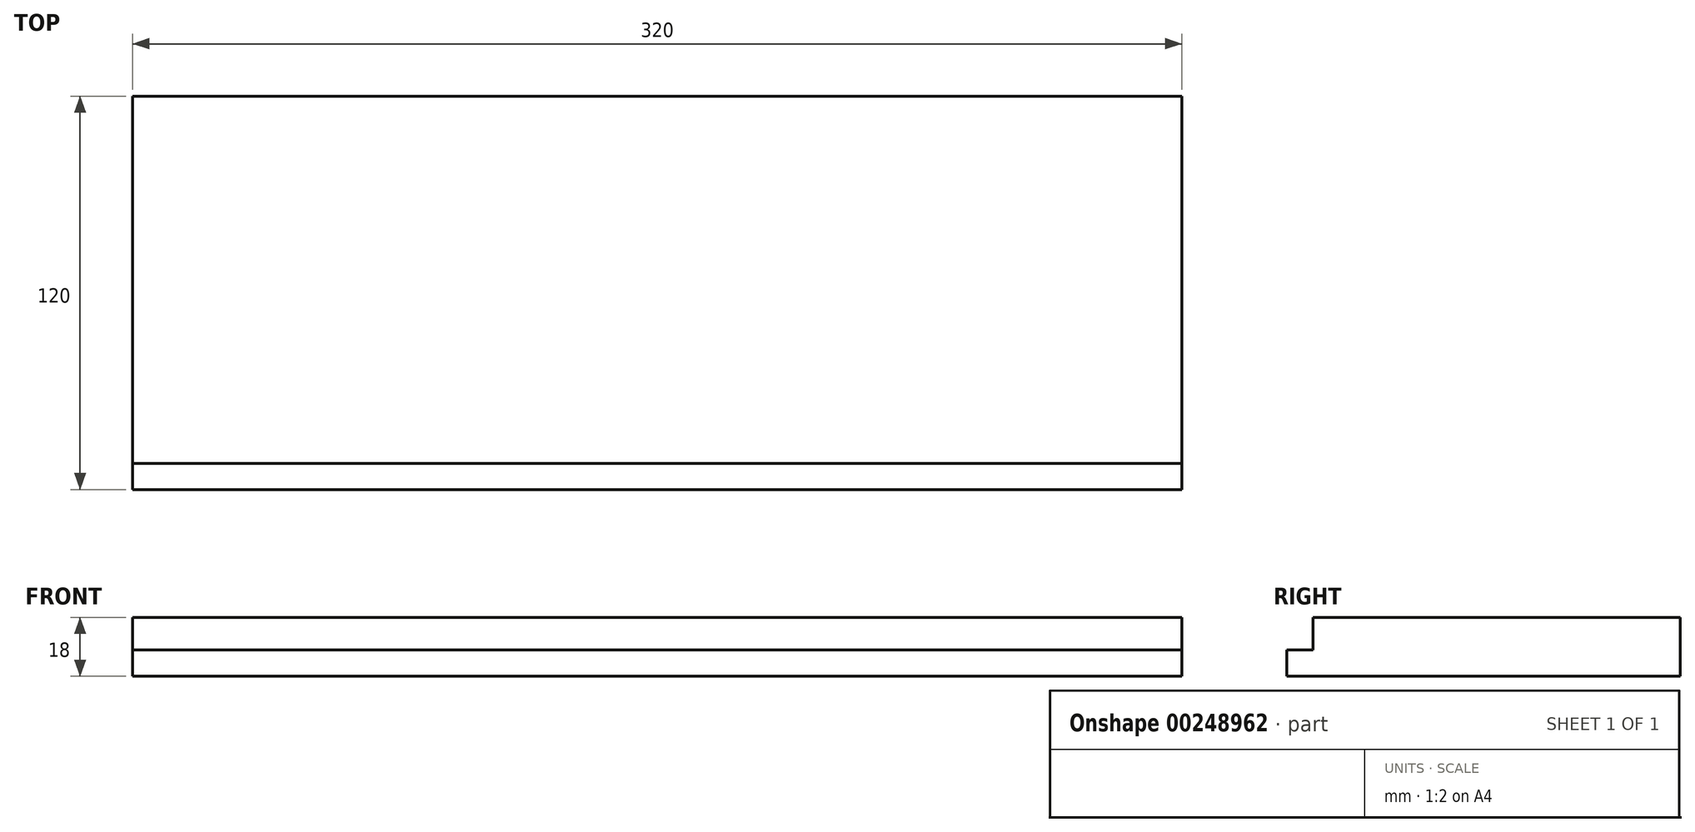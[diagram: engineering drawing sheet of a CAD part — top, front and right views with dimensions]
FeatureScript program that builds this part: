
annotation { "Feature Type Name" : "Feature", "Feature Type Description" : "" }
export const myFeature = defineFeature(function(context is Context, id is Id, definition is map)
    precondition{}
    {
        {
            var Q0;
            Q0=qCreatedBy(makeId("Top.planeOp"),FACE);
            var sketch = newSketch(context, id + "F0", { "sketchPlane" : qUnion([Q0])});
            skLineSegment(sketch, "E0.bottom", {"start": v(-160, -60) * mm, "end": v(160, -60) * mm});
            skLineSegment(sketch, "E0.top", {"start": v(-160, 60) * mm, "end": v(160, 60) * mm});
            skLineSegment(sketch, "E0.left", {"start": v(-160, 60) * mm, "end": v(-160, -60) * mm});
            skLineSegment(sketch, "E0.right", {"start": v(160, 60) * mm, "end": v(160, -60) * mm});
            skPoint(sketch, "E1", {"position": v(160, 0) * mm});
            skPoint(sketch, "E2", {"position": v(0, 60) * mm});
            skSolve(sketch);
        }
        {
            var Q0;
            Q0 = qSketchRegion(id + "F0", true);
            extrude(context, id + "F1", {"entities" : qUnion([Q0]), "depth" : 18 * mm});
        }
        {
            var Q0;
            Q0=makeQuery(id+"F1.opExtrude","SWEPT_FACE",FACE,{"disambiguationData":[OSD([sQuery(id+"F0.wireOp",EDGE,"E0.bottom")])]});
            var sketch = newSketch(context, id + "F2", { "sketchPlane" : qUnion([Q0])});
            skLineSegment(sketch, "E3.0", {"start": v(-160, 18) * mm, "end": v(160, 18) * mm});
            skLineSegment(sketch, "E4", {"start": v(-160, 18) * mm, "end": v(-160, 8) * mm});
            skLineSegment(sketch, "E5", {"start": v(-160, 8) * mm, "end": v(160, 8) * mm});
            skLineSegment(sketch, "E6", {"start": v(160, 8) * mm, "end": v(160, 18) * mm});
            skSolve(sketch);
        }
        {
            var Q0;
            Q0 = qSketchRegion(id + "F2", true);
            extrude(context, id + "F3", {"entities" : qUnion([Q0]), "operationType" : NewBodyOperationType.REMOVE, "oppositeDirection" : true, "depth" : 8 * mm});
        }
    });
